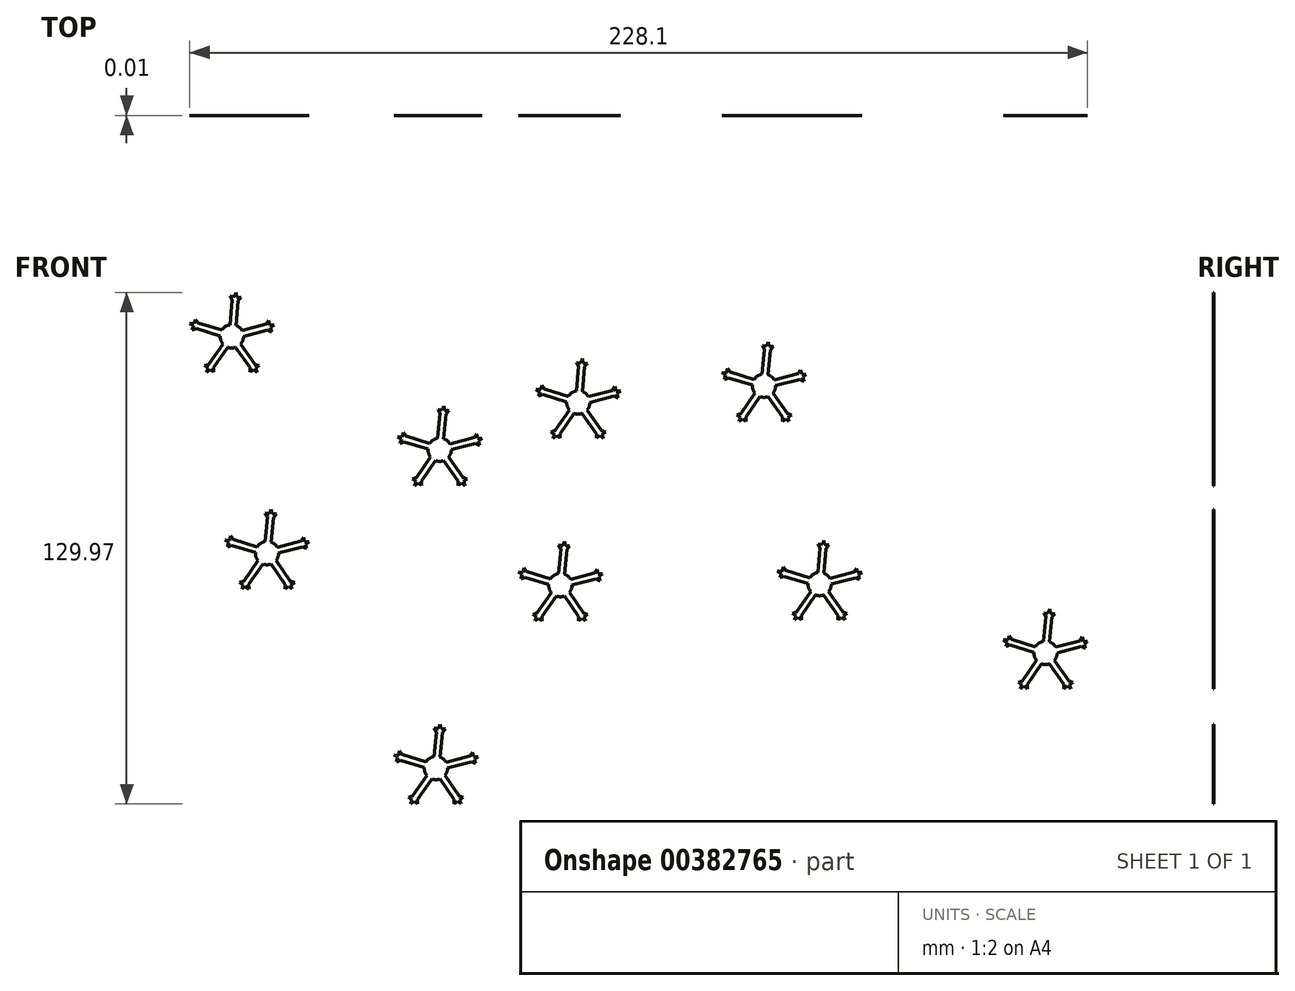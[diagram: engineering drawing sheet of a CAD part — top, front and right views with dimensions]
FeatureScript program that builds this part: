
annotation { "Feature Type Name" : "Feature", "Feature Type Description" : "" }
export const myFeature = defineFeature(function(context is Context, id is Id, definition is map)
    precondition{}
    {
        {
            var Q0;
            Q0=qCreatedBy(makeId("Front.planeOp"),FACE);
            var sketch = newSketch(context, id + "F0", { "sketchPlane" : qUnion([Q0])});
            skLineSegment(sketch, "E0", {"start": v(20.66, -9.4) * mm, "end": v(21.26, -3.1) * mm});
            skLineSegment(sketch, "E1", {"start": v(22.17, -9.55) * mm, "end": v(22.78, -3.26) * mm});
            skLineSegment(sketch, "E2", {"start": v(23.72, -10.87) * mm, "end": v(29.84, -9.26) * mm});
            skLineSegment(sketch, "E3", {"start": v(24.1, -12.34) * mm, "end": v(30.23, -10.74) * mm});
            skLineSegment(sketch, "E4", {"start": v(18.17, -12.22) * mm, "end": v(12.13, -10.36) * mm});
            skLineSegment(sketch, "E5", {"start": v(18.62, -10.76) * mm, "end": v(12.58, -8.9) * mm});
            skLineSegment(sketch, "E6", {"start": v(18.87, -14.25) * mm, "end": v(15.25, -19.44) * mm});
            skLineSegment(sketch, "E7", {"start": v(20.12, -15.12) * mm, "end": v(16.5, -20.31) * mm});
            skLineSegment(sketch, "E8", {"start": v(22.16, -15.12) * mm, "end": v(25.78, -20.31) * mm});
            skLineSegment(sketch, "E9", {"start": v(23.4, -14.25) * mm, "end": v(27.03, -19.44) * mm});
            skArc(sketch, "E10.trimOffspring", {"start": v(23.72, -10.87) * mm, "mid": v(23.06, -10.08) * mm, "end": v(22.17, -9.55) * mm});
            skArc(sketch, "E11.trimOffspring", {"start": v(23.4, -14.25) * mm, "mid": v(23.92, -13.36) * mm, "end": v(24.1, -12.34) * mm});
            skArc(sketch, "E12.trimOffspring", {"start": v(20.12, -15.12) * mm, "mid": v(21.14, -15.3) * mm, "end": v(22.16, -15.12) * mm});
            skArc(sketch, "E13.trimOffspring", {"start": v(18.17, -12.22) * mm, "mid": v(18.33, -13.3) * mm, "end": v(18.87, -14.25) * mm});
            skArc(sketch, "E14.trimOffspring", {"start": v(20.66, -9.4) * mm, "mid": v(19.5, -9.87) * mm, "end": v(18.62, -10.76) * mm});
            skLineSegment(sketch, "E15", {"start": v(21.26, -3.1) * mm, "end": v(22.78, -3.26) * mm});
            skLineSegment(sketch, "E16", {"start": v(29.84, -9.26) * mm, "end": v(30.46, -8.34) * mm});
            skLineSegment(sketch, "E17", {"start": v(30.46, -8.34) * mm, "end": v(30.73, -9.42) * mm});
            skLineSegment(sketch, "E18", {"start": v(30.73, -9.42) * mm, "end": v(31.84, -9.45) * mm});
            skLineSegment(sketch, "E19", {"start": v(31.84, -9.45) * mm, "end": v(30.96, -10.14) * mm});
            skLineSegment(sketch, "E20", {"start": v(30.96, -10.14) * mm, "end": v(31.23, -11.22) * mm});
            skLineSegment(sketch, "E21", {"start": v(31.23, -11.22) * mm, "end": v(30.23, -10.74) * mm});
            skLineSegment(sketch, "E22", {"start": v(21.26, -3.1) * mm, "end": v(20.7, -2.15) * mm});
            skLineSegment(sketch, "E23", {"start": v(20.7, -2.15) * mm, "end": v(21.8, -2.26) * mm});
            skLineSegment(sketch, "E24", {"start": v(21.8, -2.26) * mm, "end": v(22.2, -1.22) * mm});
            skLineSegment(sketch, "E25", {"start": v(22.2, -1.22) * mm, "end": v(22.4, -2.31) * mm});
            skLineSegment(sketch, "E26", {"start": v(22.4, -2.31) * mm, "end": v(23.52, -2.42) * mm});
            skLineSegment(sketch, "E27", {"start": v(23.52, -2.42) * mm, "end": v(22.78, -3.26) * mm});
            skLineSegment(sketch, "E28", {"start": v(25.78, -20.31) * mm, "end": v(27.03, -19.44) * mm});
            skLineSegment(sketch, "E29", {"start": v(27.03, -19.44) * mm, "end": v(28.08, -19.8) * mm});
            skLineSegment(sketch, "E30", {"start": v(28.08, -19.8) * mm, "end": v(27.17, -20.44) * mm});
            skLineSegment(sketch, "E31", {"start": v(27.17, -20.44) * mm, "end": v(27.53, -21.5) * mm});
            skLineSegment(sketch, "E32", {"start": v(27.53, -21.5) * mm, "end": v(26.67, -20.79) * mm});
            skLineSegment(sketch, "E33", {"start": v(26.67, -20.79) * mm, "end": v(25.76, -21.43) * mm});
            skLineSegment(sketch, "E34", {"start": v(25.76, -21.43) * mm, "end": v(25.78, -20.31) * mm});
            skLineSegment(sketch, "E35", {"start": v(29.84, -9.26) * mm, "end": v(30.23, -10.74) * mm});
            skLineSegment(sketch, "E36", {"start": v(12.58, -8.9) * mm, "end": v(12.13, -10.36) * mm});
            skLineSegment(sketch, "E37", {"start": v(15.25, -19.44) * mm, "end": v(16.5, -20.31) * mm});
            skLineSegment(sketch, "E38", {"start": v(12.58, -8.9) * mm, "end": v(11.9, -8) * mm});
            skLineSegment(sketch, "E39", {"start": v(11.9, -8) * mm, "end": v(11.58, -9.07) * mm});
            skLineSegment(sketch, "E40", {"start": v(11.58, -9.07) * mm, "end": v(10.47, -9.05) * mm});
            skLineSegment(sketch, "E41", {"start": v(10.47, -9.05) * mm, "end": v(11.4, -9.65) * mm});
            skLineSegment(sketch, "E42", {"start": v(11.4, -9.65) * mm, "end": v(11.07, -10.72) * mm});
            skLineSegment(sketch, "E43", {"start": v(11.07, -10.72) * mm, "end": v(12.13, -10.36) * mm});
            skLineSegment(sketch, "E44", {"start": v(15.25, -19.44) * mm, "end": v(14.2, -19.8) * mm});
            skLineSegment(sketch, "E45", {"start": v(14.2, -19.8) * mm, "end": v(15.11, -20.44) * mm});
            skLineSegment(sketch, "E46", {"start": v(15.11, -20.44) * mm, "end": v(14.75, -21.5) * mm});
            skLineSegment(sketch, "E47", {"start": v(14.75, -21.5) * mm, "end": v(15.61, -20.79) * mm});
            skLineSegment(sketch, "E48", {"start": v(15.61, -20.79) * mm, "end": v(16.52, -21.43) * mm});
            skLineSegment(sketch, "E49", {"start": v(16.52, -21.43) * mm, "end": v(16.5, -20.31) * mm});
            skLineSegment(sketch, "E50", {"start": v(-26.55, -13.68) * mm, "end": v(-25.95, -7.38) * mm});
            skLineSegment(sketch, "E51", {"start": v(-25.03, -13.82) * mm, "end": v(-24.43, -7.52) * mm});
            skLineSegment(sketch, "E52", {"start": v(-23.49, -15.14) * mm, "end": v(-17.37, -13.53) * mm});
            skLineSegment(sketch, "E53", {"start": v(-23.1, -16.61) * mm, "end": v(-16.98, -15) * mm});
            skLineSegment(sketch, "E54", {"start": v(-29.03, -16.49) * mm, "end": v(-35.08, -14.62) * mm});
            skLineSegment(sketch, "E55", {"start": v(-28.58, -15.03) * mm, "end": v(-34.63, -13.17) * mm});
            skLineSegment(sketch, "E56", {"start": v(-28.33, -18.52) * mm, "end": v(-31.95, -23.7) * mm});
            skLineSegment(sketch, "E57", {"start": v(-27.08, -19.4) * mm, "end": v(-30.7, -24.58) * mm});
            skLineSegment(sketch, "E58", {"start": v(-25.05, -19.4) * mm, "end": v(-21.43, -24.58) * mm});
            skLineSegment(sketch, "E59", {"start": v(-23.8, -18.52) * mm, "end": v(-20.18, -23.7) * mm});
            skArc(sketch, "E60.trimOffspring", {"start": v(-23.49, -15.14) * mm, "mid": v(-24.14, -14.34) * mm, "end": v(-25.03, -13.82) * mm});
            skArc(sketch, "E61.trimOffspring", {"start": v(-23.8, -18.52) * mm, "mid": v(-23.28, -17.63) * mm, "end": v(-23.1, -16.61) * mm});
            skArc(sketch, "E62.trimOffspring", {"start": v(-27.08, -19.4) * mm, "mid": v(-26.07, -19.57) * mm, "end": v(-25.05, -19.4) * mm});
            skArc(sketch, "E63.trimOffspring", {"start": v(-29.03, -16.49) * mm, "mid": v(-28.87, -17.57) * mm, "end": v(-28.33, -18.52) * mm});
            skArc(sketch, "E64.trimOffspring", {"start": v(-26.55, -13.68) * mm, "mid": v(-27.71, -14.13) * mm, "end": v(-28.58, -15.03) * mm});
            skLineSegment(sketch, "E65", {"start": v(-25.95, -7.38) * mm, "end": v(-24.43, -7.52) * mm});
            skLineSegment(sketch, "E66", {"start": v(-17.37, -13.53) * mm, "end": v(-16.75, -12.6) * mm});
            skLineSegment(sketch, "E67", {"start": v(-16.75, -12.6) * mm, "end": v(-16.48, -13.68) * mm});
            skLineSegment(sketch, "E68", {"start": v(-16.48, -13.68) * mm, "end": v(-15.37, -13.72) * mm});
            skLineSegment(sketch, "E69", {"start": v(-15.37, -13.72) * mm, "end": v(-16.24, -14.4) * mm});
            skLineSegment(sketch, "E70", {"start": v(-16.24, -14.4) * mm, "end": v(-15.97, -15.48) * mm});
            skLineSegment(sketch, "E71", {"start": v(-15.97, -15.48) * mm, "end": v(-16.98, -15) * mm});
            skLineSegment(sketch, "E72", {"start": v(-25.95, -7.38) * mm, "end": v(-26.51, -6.42) * mm});
            skLineSegment(sketch, "E73", {"start": v(-26.51, -6.42) * mm, "end": v(-25.4, -6.52) * mm});
            skLineSegment(sketch, "E74", {"start": v(-25.4, -6.52) * mm, "end": v(-25, -5.49) * mm});
            skLineSegment(sketch, "E75", {"start": v(-25, -5.49) * mm, "end": v(-24.8, -6.58) * mm});
            skLineSegment(sketch, "E76", {"start": v(-24.8, -6.58) * mm, "end": v(-23.7, -6.69) * mm});
            skLineSegment(sketch, "E77", {"start": v(-23.7, -6.69) * mm, "end": v(-24.43, -7.52) * mm});
            skLineSegment(sketch, "E78", {"start": v(-21.43, -24.58) * mm, "end": v(-20.18, -23.7) * mm});
            skLineSegment(sketch, "E79", {"start": v(-20.18, -23.7) * mm, "end": v(-19.13, -24.07) * mm});
            skLineSegment(sketch, "E80", {"start": v(-19.13, -24.07) * mm, "end": v(-20.04, -24.7) * mm});
            skLineSegment(sketch, "E81", {"start": v(-20.04, -24.7) * mm, "end": v(-19.68, -25.76) * mm});
            skLineSegment(sketch, "E82", {"start": v(-19.68, -25.76) * mm, "end": v(-20.54, -25.06) * mm});
            skLineSegment(sketch, "E83", {"start": v(-20.54, -25.06) * mm, "end": v(-21.45, -25.7) * mm});
            skLineSegment(sketch, "E84", {"start": v(-21.45, -25.7) * mm, "end": v(-21.43, -24.58) * mm});
            skLineSegment(sketch, "E85", {"start": v(-17.37, -13.53) * mm, "end": v(-16.98, -15) * mm});
            skLineSegment(sketch, "E86", {"start": v(-34.63, -13.17) * mm, "end": v(-35.08, -14.62) * mm});
            skLineSegment(sketch, "E87", {"start": v(-31.95, -23.7) * mm, "end": v(-30.7, -24.58) * mm});
            skLineSegment(sketch, "E88", {"start": v(-34.63, -13.17) * mm, "end": v(-35.3, -12.28) * mm});
            skLineSegment(sketch, "E89", {"start": v(-35.3, -12.28) * mm, "end": v(-35.63, -13.34) * mm});
            skLineSegment(sketch, "E90", {"start": v(-35.63, -13.34) * mm, "end": v(-36.74, -13.31) * mm});
            skLineSegment(sketch, "E91", {"start": v(-36.74, -13.31) * mm, "end": v(-35.8, -13.92) * mm});
            skLineSegment(sketch, "E92", {"start": v(-35.8, -13.92) * mm, "end": v(-36.13, -14.98) * mm});
            skLineSegment(sketch, "E93", {"start": v(-36.13, -14.98) * mm, "end": v(-35.08, -14.62) * mm});
            skLineSegment(sketch, "E94", {"start": v(-31.95, -23.7) * mm, "end": v(-33, -24.07) * mm});
            skLineSegment(sketch, "E95", {"start": v(-33, -24.07) * mm, "end": v(-32.1, -24.7) * mm});
            skLineSegment(sketch, "E96", {"start": v(-32.1, -24.7) * mm, "end": v(-32.46, -25.76) * mm});
            skLineSegment(sketch, "E97", {"start": v(-32.46, -25.76) * mm, "end": v(-31.6, -25.06) * mm});
            skLineSegment(sketch, "E98", {"start": v(-31.6, -25.06) * mm, "end": v(-30.68, -25.7) * mm});
            skLineSegment(sketch, "E99", {"start": v(-30.68, -25.7) * mm, "end": v(-30.7, -24.58) * mm});
            skLineSegment(sketch, "E100", {"start": v(-61.75, -25.68) * mm, "end": v(-61.15, -19.38) * mm});
            skLineSegment(sketch, "E101", {"start": v(-60.24, -25.82) * mm, "end": v(-59.63, -19.52) * mm});
            skLineSegment(sketch, "E102", {"start": v(-58.69, -27.14) * mm, "end": v(-52.57, -25.53) * mm});
            skLineSegment(sketch, "E103", {"start": v(-58.3, -28.61) * mm, "end": v(-52.18, -27) * mm});
            skLineSegment(sketch, "E104", {"start": v(-64.24, -28.49) * mm, "end": v(-70.28, -26.63) * mm});
            skLineSegment(sketch, "E105", {"start": v(-63.79, -27.03) * mm, "end": v(-69.83, -25.17) * mm});
            skLineSegment(sketch, "E106", {"start": v(-63.54, -30.52) * mm, "end": v(-67.16, -35.7) * mm});
            skLineSegment(sketch, "E107", {"start": v(-62.29, -31.4) * mm, "end": v(-65.9, -36.58) * mm});
            skLineSegment(sketch, "E108", {"start": v(-60.25, -31.4) * mm, "end": v(-56.63, -36.58) * mm});
            skLineSegment(sketch, "E109", {"start": v(-59, -30.52) * mm, "end": v(-55.38, -35.7) * mm});
            skArc(sketch, "E110.trimOffspring", {"start": v(-58.69, -27.14) * mm, "mid": v(-59.35, -26.34) * mm, "end": v(-60.24, -25.82) * mm});
            skArc(sketch, "E111.trimOffspring", {"start": v(-59, -30.52) * mm, "mid": v(-58.49, -29.63) * mm, "end": v(-58.3, -28.61) * mm});
            skArc(sketch, "E112.trimOffspring", {"start": v(-62.29, -31.4) * mm, "mid": v(-61.27, -31.57) * mm, "end": v(-60.25, -31.4) * mm});
            skArc(sketch, "E113.trimOffspring", {"start": v(-64.24, -28.49) * mm, "mid": v(-64.08, -29.57) * mm, "end": v(-63.54, -30.52) * mm});
            skArc(sketch, "E114.trimOffspring", {"start": v(-61.75, -25.68) * mm, "mid": v(-62.92, -26.14) * mm, "end": v(-63.79, -27.03) * mm});
            skLineSegment(sketch, "E115", {"start": v(-61.15, -19.38) * mm, "end": v(-59.63, -19.52) * mm});
            skLineSegment(sketch, "E116", {"start": v(-52.57, -25.53) * mm, "end": v(-51.95, -24.6) * mm});
            skLineSegment(sketch, "E117", {"start": v(-51.95, -24.6) * mm, "end": v(-51.68, -25.69) * mm});
            skLineSegment(sketch, "E118", {"start": v(-51.68, -25.69) * mm, "end": v(-50.57, -25.72) * mm});
            skLineSegment(sketch, "E119", {"start": v(-50.57, -25.72) * mm, "end": v(-51.45, -26.4) * mm});
            skLineSegment(sketch, "E120", {"start": v(-51.45, -26.4) * mm, "end": v(-51.18, -27.49) * mm});
            skLineSegment(sketch, "E121", {"start": v(-51.18, -27.49) * mm, "end": v(-52.18, -27) * mm});
            skLineSegment(sketch, "E122", {"start": v(-61.15, -19.38) * mm, "end": v(-61.72, -18.42) * mm});
            skLineSegment(sketch, "E123", {"start": v(-61.72, -18.42) * mm, "end": v(-60.6, -18.53) * mm});
            skLineSegment(sketch, "E124", {"start": v(-60.6, -18.53) * mm, "end": v(-60.2, -17.49) * mm});
            skLineSegment(sketch, "E125", {"start": v(-60.2, -17.49) * mm, "end": v(-60, -18.58) * mm});
            skLineSegment(sketch, "E126", {"start": v(-60, -18.58) * mm, "end": v(-58.9, -18.69) * mm});
            skLineSegment(sketch, "E127", {"start": v(-58.9, -18.69) * mm, "end": v(-59.63, -19.52) * mm});
            skLineSegment(sketch, "E128", {"start": v(-56.63, -36.58) * mm, "end": v(-55.38, -35.7) * mm});
            skLineSegment(sketch, "E129", {"start": v(-55.38, -35.7) * mm, "end": v(-54.33, -36.07) * mm});
            skLineSegment(sketch, "E130", {"start": v(-54.33, -36.07) * mm, "end": v(-55.24, -36.71) * mm});
            skLineSegment(sketch, "E131", {"start": v(-55.24, -36.71) * mm, "end": v(-54.88, -37.76) * mm});
            skLineSegment(sketch, "E132", {"start": v(-54.88, -37.76) * mm, "end": v(-55.74, -37.06) * mm});
            skLineSegment(sketch, "E133", {"start": v(-55.74, -37.06) * mm, "end": v(-56.66, -37.7) * mm});
            skLineSegment(sketch, "E134", {"start": v(-56.66, -37.7) * mm, "end": v(-56.63, -36.58) * mm});
            skLineSegment(sketch, "E135", {"start": v(-52.57, -25.53) * mm, "end": v(-52.18, -27) * mm});
            skLineSegment(sketch, "E136", {"start": v(-69.83, -25.17) * mm, "end": v(-70.28, -26.63) * mm});
            skLineSegment(sketch, "E137", {"start": v(-67.16, -35.7) * mm, "end": v(-65.9, -36.58) * mm});
            skLineSegment(sketch, "E138", {"start": v(-69.83, -25.17) * mm, "end": v(-70.5, -24.28) * mm});
            skLineSegment(sketch, "E139", {"start": v(-70.5, -24.28) * mm, "end": v(-70.83, -25.34) * mm});
            skLineSegment(sketch, "E140", {"start": v(-70.83, -25.34) * mm, "end": v(-71.94, -25.32) * mm});
            skLineSegment(sketch, "E141", {"start": v(-71.94, -25.32) * mm, "end": v(-71, -25.92) * mm});
            skLineSegment(sketch, "E142", {"start": v(-71, -25.92) * mm, "end": v(-71.34, -26.99) * mm});
            skLineSegment(sketch, "E143", {"start": v(-71.34, -26.99) * mm, "end": v(-70.28, -26.63) * mm});
            skLineSegment(sketch, "E144", {"start": v(-67.16, -35.7) * mm, "end": v(-68.2, -36.07) * mm});
            skLineSegment(sketch, "E145", {"start": v(-68.2, -36.07) * mm, "end": v(-67.3, -36.71) * mm});
            skLineSegment(sketch, "E146", {"start": v(-67.3, -36.71) * mm, "end": v(-67.66, -37.76) * mm});
            skLineSegment(sketch, "E147", {"start": v(-67.66, -37.76) * mm, "end": v(-66.8, -37.06) * mm});
            skLineSegment(sketch, "E148", {"start": v(-66.8, -37.06) * mm, "end": v(-65.89, -37.7) * mm});
            skLineSegment(sketch, "E149", {"start": v(-65.89, -37.7) * mm, "end": v(-65.9, -36.58) * mm});
            skLineSegment(sketch, "E150", {"start": v(-114.56, 3.13) * mm, "end": v(-113.96, 9.43) * mm});
            skLineSegment(sketch, "E151", {"start": v(-113.04, 2.98) * mm, "end": v(-112.44, 9.28) * mm});
            skLineSegment(sketch, "E152", {"start": v(-111.5, 1.66) * mm, "end": v(-105.38, 3.27) * mm});
            skLineSegment(sketch, "E153", {"start": v(-111.1, 0.2) * mm, "end": v(-104.99, 1.8) * mm});
            skLineSegment(sketch, "E154", {"start": v(-117.04, 0.32) * mm, "end": v(-123.09, 2.18) * mm});
            skLineSegment(sketch, "E155", {"start": v(-116.6, 1.77) * mm, "end": v(-122.64, 3.63) * mm});
            skLineSegment(sketch, "E156", {"start": v(-116.34, -1.72) * mm, "end": v(-119.96, -6.9) * mm});
            skLineSegment(sketch, "E157", {"start": v(-115.1, -2.59) * mm, "end": v(-118.71, -7.78) * mm});
            skLineSegment(sketch, "E158", {"start": v(-113.06, -2.59) * mm, "end": v(-109.44, -7.78) * mm});
            skLineSegment(sketch, "E159", {"start": v(-111.81, -1.72) * mm, "end": v(-108.2, -6.9) * mm});
            skArc(sketch, "E160.trimOffspring", {"start": v(-111.5, 1.66) * mm, "mid": v(-112.15, 2.46) * mm, "end": v(-113.04, 2.98) * mm});
            skArc(sketch, "E161.trimOffspring", {"start": v(-111.81, -1.72) * mm, "mid": v(-111.3, -0.82) * mm, "end": v(-111.1, 0.2) * mm});
            skArc(sketch, "E162.trimOffspring", {"start": v(-115.1, -2.59) * mm, "mid": v(-114.08, -2.77) * mm, "end": v(-113.06, -2.59) * mm});
            skArc(sketch, "E163.trimOffspring", {"start": v(-117.04, 0.32) * mm, "mid": v(-116.88, -0.77) * mm, "end": v(-116.34, -1.72) * mm});
            skArc(sketch, "E164.trimOffspring", {"start": v(-114.56, 3.13) * mm, "mid": v(-115.72, 2.67) * mm, "end": v(-116.6, 1.77) * mm});
            skLineSegment(sketch, "E165", {"start": v(-113.96, 9.43) * mm, "end": v(-112.44, 9.28) * mm});
            skLineSegment(sketch, "E166", {"start": v(-105.38, 3.27) * mm, "end": v(-104.76, 4.2) * mm});
            skLineSegment(sketch, "E167", {"start": v(-104.76, 4.2) * mm, "end": v(-104.5, 3.12) * mm});
            skLineSegment(sketch, "E168", {"start": v(-104.5, 3.12) * mm, "end": v(-103.38, 3.08) * mm});
            skLineSegment(sketch, "E169", {"start": v(-103.38, 3.08) * mm, "end": v(-104.25, 2.4) * mm});
            skLineSegment(sketch, "E170", {"start": v(-104.25, 2.4) * mm, "end": v(-103.98, 1.32) * mm});
            skLineSegment(sketch, "E171", {"start": v(-103.98, 1.32) * mm, "end": v(-104.99, 1.8) * mm});
            skLineSegment(sketch, "E172", {"start": v(-113.96, 9.43) * mm, "end": v(-114.52, 10.38) * mm});
            skLineSegment(sketch, "E173", {"start": v(-114.52, 10.38) * mm, "end": v(-113.41, 10.28) * mm});
            skLineSegment(sketch, "E174", {"start": v(-113.41, 10.28) * mm, "end": v(-113, 11.32) * mm});
            skLineSegment(sketch, "E175", {"start": v(-113, 11.32) * mm, "end": v(-112.81, 10.22) * mm});
            skLineSegment(sketch, "E176", {"start": v(-112.81, 10.22) * mm, "end": v(-111.7, 10.11) * mm});
            skLineSegment(sketch, "E177", {"start": v(-111.7, 10.11) * mm, "end": v(-112.44, 9.28) * mm});
            skLineSegment(sketch, "E178", {"start": v(-109.44, -7.78) * mm, "end": v(-108.2, -6.9) * mm});
            skLineSegment(sketch, "E179", {"start": v(-108.2, -6.9) * mm, "end": v(-107.14, -7.27) * mm});
            skLineSegment(sketch, "E180", {"start": v(-107.14, -7.27) * mm, "end": v(-108.05, -7.9) * mm});
            skLineSegment(sketch, "E181", {"start": v(-108.05, -7.9) * mm, "end": v(-107.69, -8.96) * mm});
            skLineSegment(sketch, "E182", {"start": v(-107.69, -8.96) * mm, "end": v(-108.55, -8.25) * mm});
            skLineSegment(sketch, "E183", {"start": v(-108.55, -8.25) * mm, "end": v(-109.46, -8.9) * mm});
            skLineSegment(sketch, "E184", {"start": v(-109.46, -8.9) * mm, "end": v(-109.44, -7.78) * mm});
            skLineSegment(sketch, "E185", {"start": v(-105.38, 3.27) * mm, "end": v(-104.99, 1.8) * mm});
            skLineSegment(sketch, "E186", {"start": v(-122.64, 3.63) * mm, "end": v(-123.09, 2.18) * mm});
            skLineSegment(sketch, "E187", {"start": v(-119.96, -6.9) * mm, "end": v(-118.71, -7.78) * mm});
            skLineSegment(sketch, "E188", {"start": v(-122.64, 3.63) * mm, "end": v(-123.3, 4.53) * mm});
            skLineSegment(sketch, "E189", {"start": v(-123.3, 4.53) * mm, "end": v(-123.64, 3.46) * mm});
            skLineSegment(sketch, "E190", {"start": v(-123.64, 3.46) * mm, "end": v(-124.75, 3.49) * mm});
            skLineSegment(sketch, "E191", {"start": v(-124.75, 3.49) * mm, "end": v(-123.81, 2.88) * mm});
            skLineSegment(sketch, "E192", {"start": v(-123.81, 2.88) * mm, "end": v(-124.14, 1.82) * mm});
            skLineSegment(sketch, "E193", {"start": v(-124.14, 1.82) * mm, "end": v(-123.09, 2.18) * mm});
            skLineSegment(sketch, "E194", {"start": v(-119.96, -6.9) * mm, "end": v(-121.02, -7.27) * mm});
            skLineSegment(sketch, "E195", {"start": v(-121.02, -7.27) * mm, "end": v(-120.1, -7.9) * mm});
            skLineSegment(sketch, "E196", {"start": v(-120.1, -7.9) * mm, "end": v(-120.47, -8.96) * mm});
            skLineSegment(sketch, "E197", {"start": v(-120.47, -8.96) * mm, "end": v(-119.6, -8.25) * mm});
            skLineSegment(sketch, "E198", {"start": v(-119.6, -8.25) * mm, "end": v(-118.7, -8.9) * mm});
            skLineSegment(sketch, "E199", {"start": v(-118.7, -8.9) * mm, "end": v(-118.71, -7.78) * mm});
            skLineSegment(sketch, "E200", {"start": v(34.8, -59.81) * mm, "end": v(35.4, -53.52) * mm});
            skLineSegment(sketch, "E201", {"start": v(36.3, -59.96) * mm, "end": v(36.91, -53.66) * mm});
            skLineSegment(sketch, "E202", {"start": v(37.86, -61.28) * mm, "end": v(43.98, -59.67) * mm});
            skLineSegment(sketch, "E203", {"start": v(38.24, -62.75) * mm, "end": v(44.36, -61.14) * mm});
            skLineSegment(sketch, "E204", {"start": v(32.31, -62.63) * mm, "end": v(26.26, -60.76) * mm});
            skLineSegment(sketch, "E205", {"start": v(32.76, -61.17) * mm, "end": v(26.71, -59.3) * mm});
            skLineSegment(sketch, "E206", {"start": v(33, -64.66) * mm, "end": v(29.39, -69.85) * mm});
            skLineSegment(sketch, "E207", {"start": v(34.26, -65.53) * mm, "end": v(30.64, -70.72) * mm});
            skLineSegment(sketch, "E208", {"start": v(36.3, -65.53) * mm, "end": v(39.91, -70.72) * mm});
            skLineSegment(sketch, "E209", {"start": v(37.54, -64.66) * mm, "end": v(41.16, -69.85) * mm});
            skArc(sketch, "E210.trimOffspring", {"start": v(37.86, -61.28) * mm, "mid": v(37.2, -60.48) * mm, "end": v(36.3, -59.96) * mm});
            skArc(sketch, "E211.trimOffspring", {"start": v(37.54, -64.66) * mm, "mid": v(38.06, -63.77) * mm, "end": v(38.24, -62.75) * mm});
            skArc(sketch, "E212.trimOffspring", {"start": v(34.26, -65.53) * mm, "mid": v(35.28, -65.7) * mm, "end": v(36.3, -65.53) * mm});
            skArc(sketch, "E213.trimOffspring", {"start": v(32.31, -62.63) * mm, "mid": v(32.47, -63.7) * mm, "end": v(33, -64.66) * mm});
            skArc(sketch, "E214.trimOffspring", {"start": v(34.8, -59.81) * mm, "mid": v(33.63, -60.27) * mm, "end": v(32.76, -61.17) * mm});
            skLineSegment(sketch, "E215", {"start": v(35.4, -53.52) * mm, "end": v(36.91, -53.66) * mm});
            skLineSegment(sketch, "E216", {"start": v(43.98, -59.67) * mm, "end": v(44.6, -58.74) * mm});
            skLineSegment(sketch, "E217", {"start": v(44.6, -58.74) * mm, "end": v(44.86, -59.82) * mm});
            skLineSegment(sketch, "E218", {"start": v(44.86, -59.82) * mm, "end": v(45.97, -59.86) * mm});
            skLineSegment(sketch, "E219", {"start": v(45.97, -59.86) * mm, "end": v(45.1, -60.54) * mm});
            skLineSegment(sketch, "E220", {"start": v(45.1, -60.54) * mm, "end": v(45.37, -61.62) * mm});
            skLineSegment(sketch, "E221", {"start": v(45.37, -61.62) * mm, "end": v(44.36, -61.14) * mm});
            skLineSegment(sketch, "E222", {"start": v(35.4, -53.52) * mm, "end": v(34.83, -52.56) * mm});
            skLineSegment(sketch, "E223", {"start": v(34.83, -52.56) * mm, "end": v(35.94, -52.66) * mm});
            skLineSegment(sketch, "E224", {"start": v(35.94, -52.66) * mm, "end": v(36.34, -51.63) * mm});
            skLineSegment(sketch, "E225", {"start": v(36.34, -51.63) * mm, "end": v(36.54, -52.72) * mm});
            skLineSegment(sketch, "E226", {"start": v(36.54, -52.72) * mm, "end": v(37.65, -52.83) * mm});
            skLineSegment(sketch, "E227", {"start": v(37.65, -52.83) * mm, "end": v(36.91, -53.66) * mm});
            skLineSegment(sketch, "E228", {"start": v(39.91, -70.72) * mm, "end": v(41.16, -69.85) * mm});
            skLineSegment(sketch, "E229", {"start": v(41.16, -69.85) * mm, "end": v(42.21, -70.21) * mm});
            skLineSegment(sketch, "E230", {"start": v(42.21, -70.21) * mm, "end": v(41.3, -70.85) * mm});
            skLineSegment(sketch, "E231", {"start": v(41.3, -70.85) * mm, "end": v(41.67, -71.9) * mm});
            skLineSegment(sketch, "E232", {"start": v(41.67, -71.9) * mm, "end": v(40.8, -71.2) * mm});
            skLineSegment(sketch, "E233", {"start": v(40.8, -71.2) * mm, "end": v(39.9, -71.83) * mm});
            skLineSegment(sketch, "E234", {"start": v(39.9, -71.83) * mm, "end": v(39.91, -70.72) * mm});
            skLineSegment(sketch, "E235", {"start": v(43.98, -59.67) * mm, "end": v(44.36, -61.14) * mm});
            skLineSegment(sketch, "E236", {"start": v(26.71, -59.3) * mm, "end": v(26.26, -60.76) * mm});
            skLineSegment(sketch, "E237", {"start": v(29.39, -69.85) * mm, "end": v(30.64, -70.72) * mm});
            skLineSegment(sketch, "E238", {"start": v(26.71, -59.3) * mm, "end": v(26.04, -58.42) * mm});
            skLineSegment(sketch, "E239", {"start": v(26.04, -58.42) * mm, "end": v(25.72, -59.48) * mm});
            skLineSegment(sketch, "E240", {"start": v(25.72, -59.48) * mm, "end": v(24.6, -59.45) * mm});
            skLineSegment(sketch, "E241", {"start": v(24.6, -59.45) * mm, "end": v(25.54, -60.06) * mm});
            skLineSegment(sketch, "E242", {"start": v(25.54, -60.06) * mm, "end": v(25.2, -61.12) * mm});
            skLineSegment(sketch, "E243", {"start": v(25.2, -61.12) * mm, "end": v(26.26, -60.76) * mm});
            skLineSegment(sketch, "E244", {"start": v(29.39, -69.85) * mm, "end": v(28.34, -70.21) * mm});
            skLineSegment(sketch, "E245", {"start": v(28.34, -70.21) * mm, "end": v(29.25, -70.85) * mm});
            skLineSegment(sketch, "E246", {"start": v(29.25, -70.85) * mm, "end": v(28.89, -71.9) * mm});
            skLineSegment(sketch, "E247", {"start": v(28.89, -71.9) * mm, "end": v(29.75, -71.2) * mm});
            skLineSegment(sketch, "E248", {"start": v(29.75, -71.2) * mm, "end": v(30.66, -71.83) * mm});
            skLineSegment(sketch, "E249", {"start": v(30.66, -71.83) * mm, "end": v(30.64, -70.72) * mm});
            skLineSegment(sketch, "E250", {"start": v(-31.08, -60.08) * mm, "end": v(-30.48, -53.78) * mm});
            skLineSegment(sketch, "E251", {"start": v(-29.57, -60.23) * mm, "end": v(-28.96, -53.93) * mm});
            skLineSegment(sketch, "E252", {"start": v(-28.02, -61.54) * mm, "end": v(-21.9, -59.94) * mm});
            skLineSegment(sketch, "E253", {"start": v(-27.63, -63.02) * mm, "end": v(-21.51, -61.41) * mm});
            skLineSegment(sketch, "E254", {"start": v(-33.56, -62.9) * mm, "end": v(-39.61, -61.03) * mm});
            skLineSegment(sketch, "E255", {"start": v(-33.12, -61.44) * mm, "end": v(-39.16, -59.57) * mm});
            skLineSegment(sketch, "E256", {"start": v(-32.87, -64.92) * mm, "end": v(-36.49, -70.11) * mm});
            skLineSegment(sketch, "E257", {"start": v(-31.62, -65.8) * mm, "end": v(-35.24, -70.99) * mm});
            skLineSegment(sketch, "E258", {"start": v(-29.58, -65.8) * mm, "end": v(-25.96, -70.99) * mm});
            skLineSegment(sketch, "E259", {"start": v(-28.33, -64.92) * mm, "end": v(-24.71, -70.11) * mm});
            skArc(sketch, "E260.trimOffspring", {"start": v(-28.02, -61.54) * mm, "mid": v(-28.68, -60.75) * mm, "end": v(-29.57, -60.23) * mm});
            skArc(sketch, "E261.trimOffspring", {"start": v(-28.33, -64.92) * mm, "mid": v(-27.81, -64.03) * mm, "end": v(-27.63, -63.02) * mm});
            skArc(sketch, "E262.trimOffspring", {"start": v(-31.62, -65.8) * mm, "mid": v(-30.6, -65.98) * mm, "end": v(-29.58, -65.8) * mm});
            skArc(sketch, "E263.trimOffspring", {"start": v(-33.56, -62.9) * mm, "mid": v(-33.4, -63.97) * mm, "end": v(-32.87, -64.92) * mm});
            skArc(sketch, "E264.trimOffspring", {"start": v(-31.08, -60.08) * mm, "mid": v(-32.25, -60.54) * mm, "end": v(-33.12, -61.44) * mm});
            skLineSegment(sketch, "E265", {"start": v(-30.48, -53.78) * mm, "end": v(-28.96, -53.93) * mm});
            skLineSegment(sketch, "E266", {"start": v(-21.9, -59.94) * mm, "end": v(-21.28, -59) * mm});
            skLineSegment(sketch, "E267", {"start": v(-21.28, -59) * mm, "end": v(-21.01, -60.09) * mm});
            skLineSegment(sketch, "E268", {"start": v(-21.01, -60.09) * mm, "end": v(-19.9, -60.12) * mm});
            skLineSegment(sketch, "E269", {"start": v(-19.9, -60.12) * mm, "end": v(-20.78, -60.81) * mm});
            skLineSegment(sketch, "E270", {"start": v(-20.78, -60.81) * mm, "end": v(-20.5, -61.9) * mm});
            skLineSegment(sketch, "E271", {"start": v(-20.5, -61.9) * mm, "end": v(-21.51, -61.41) * mm});
            skLineSegment(sketch, "E272", {"start": v(-30.48, -53.78) * mm, "end": v(-31.04, -52.82) * mm});
            skLineSegment(sketch, "E273", {"start": v(-31.04, -52.82) * mm, "end": v(-29.94, -52.93) * mm});
            skLineSegment(sketch, "E274", {"start": v(-29.94, -52.93) * mm, "end": v(-29.53, -51.9) * mm});
            skLineSegment(sketch, "E275", {"start": v(-29.53, -51.9) * mm, "end": v(-29.33, -52.99) * mm});
            skLineSegment(sketch, "E276", {"start": v(-29.33, -52.99) * mm, "end": v(-28.22, -53.1) * mm});
            skLineSegment(sketch, "E277", {"start": v(-28.22, -53.1) * mm, "end": v(-28.96, -53.93) * mm});
            skLineSegment(sketch, "E278", {"start": v(-25.96, -70.99) * mm, "end": v(-24.71, -70.11) * mm});
            skLineSegment(sketch, "E279", {"start": v(-24.71, -70.11) * mm, "end": v(-23.66, -70.48) * mm});
            skLineSegment(sketch, "E280", {"start": v(-23.66, -70.48) * mm, "end": v(-24.57, -71.12) * mm});
            skLineSegment(sketch, "E281", {"start": v(-24.57, -71.12) * mm, "end": v(-24.2, -72.17) * mm});
            skLineSegment(sketch, "E282", {"start": v(-24.2, -72.17) * mm, "end": v(-25.07, -71.46) * mm});
            skLineSegment(sketch, "E283", {"start": v(-25.07, -71.46) * mm, "end": v(-25.98, -72.1) * mm});
            skLineSegment(sketch, "E284", {"start": v(-25.98, -72.1) * mm, "end": v(-25.96, -70.99) * mm});
            skLineSegment(sketch, "E285", {"start": v(-21.9, -59.94) * mm, "end": v(-21.51, -61.41) * mm});
            skLineSegment(sketch, "E286", {"start": v(-39.16, -59.57) * mm, "end": v(-39.61, -61.03) * mm});
            skLineSegment(sketch, "E287", {"start": v(-36.49, -70.11) * mm, "end": v(-35.24, -70.99) * mm});
            skLineSegment(sketch, "E288", {"start": v(-39.16, -59.57) * mm, "end": v(-39.83, -58.68) * mm});
            skLineSegment(sketch, "E289", {"start": v(-39.83, -58.68) * mm, "end": v(-40.16, -59.75) * mm});
            skLineSegment(sketch, "E290", {"start": v(-40.16, -59.75) * mm, "end": v(-41.27, -59.72) * mm});
            skLineSegment(sketch, "E291", {"start": v(-41.27, -59.72) * mm, "end": v(-40.34, -60.33) * mm});
            skLineSegment(sketch, "E292", {"start": v(-40.34, -60.33) * mm, "end": v(-40.67, -61.39) * mm});
            skLineSegment(sketch, "E293", {"start": v(-40.67, -61.39) * mm, "end": v(-39.61, -61.03) * mm});
            skLineSegment(sketch, "E294", {"start": v(-36.49, -70.11) * mm, "end": v(-37.54, -70.48) * mm});
            skLineSegment(sketch, "E295", {"start": v(-37.54, -70.48) * mm, "end": v(-36.63, -71.12) * mm});
            skLineSegment(sketch, "E296", {"start": v(-36.63, -71.12) * mm, "end": v(-36.99, -72.17) * mm});
            skLineSegment(sketch, "E297", {"start": v(-36.99, -72.17) * mm, "end": v(-36.13, -71.46) * mm});
            skLineSegment(sketch, "E298", {"start": v(-36.13, -71.46) * mm, "end": v(-35.21, -72.1) * mm});
            skLineSegment(sketch, "E299", {"start": v(-35.21, -72.1) * mm, "end": v(-35.24, -70.99) * mm});
            skLineSegment(sketch, "E300", {"start": v(-105.61, -51.95) * mm, "end": v(-105, -45.65) * mm});
            skLineSegment(sketch, "E301", {"start": v(-104.1, -52.1) * mm, "end": v(-103.5, -45.8) * mm});
            skLineSegment(sketch, "E302", {"start": v(-102.55, -53.41) * mm, "end": v(-96.43, -51.8) * mm});
            skLineSegment(sketch, "E303", {"start": v(-102.16, -54.88) * mm, "end": v(-96.04, -53.28) * mm});
            skLineSegment(sketch, "E304", {"start": v(-108.1, -54.76) * mm, "end": v(-114.14, -52.9) * mm});
            skLineSegment(sketch, "E305", {"start": v(-107.64, -53.3) * mm, "end": v(-113.7, -51.44) * mm});
            skLineSegment(sketch, "E306", {"start": v(-107.4, -56.8) * mm, "end": v(-111.01, -61.98) * mm});
            skLineSegment(sketch, "E307", {"start": v(-106.14, -57.66) * mm, "end": v(-109.76, -62.85) * mm});
            skLineSegment(sketch, "E308", {"start": v(-104.11, -57.66) * mm, "end": v(-100.5, -62.85) * mm});
            skLineSegment(sketch, "E309", {"start": v(-102.86, -56.8) * mm, "end": v(-99.24, -61.98) * mm});
            skArc(sketch, "E310.trimOffspring", {"start": v(-102.55, -53.41) * mm, "mid": v(-103.2, -52.62) * mm, "end": v(-104.1, -52.1) * mm});
            skArc(sketch, "E311.trimOffspring", {"start": v(-102.86, -56.8) * mm, "mid": v(-102.34, -55.9) * mm, "end": v(-102.16, -54.88) * mm});
            skArc(sketch, "E312.trimOffspring", {"start": v(-106.14, -57.66) * mm, "mid": v(-105.13, -57.84) * mm, "end": v(-104.11, -57.66) * mm});
            skArc(sketch, "E313.trimOffspring", {"start": v(-108.1, -54.76) * mm, "mid": v(-107.93, -55.84) * mm, "end": v(-107.4, -56.8) * mm});
            skArc(sketch, "E314.trimOffspring", {"start": v(-105.61, -51.95) * mm, "mid": v(-106.77, -52.4) * mm, "end": v(-107.64, -53.3) * mm});
            skLineSegment(sketch, "E315", {"start": v(-105, -45.65) * mm, "end": v(-103.5, -45.8) * mm});
            skLineSegment(sketch, "E316", {"start": v(-96.43, -51.8) * mm, "end": v(-95.81, -50.88) * mm});
            skLineSegment(sketch, "E317", {"start": v(-95.81, -50.88) * mm, "end": v(-95.54, -51.96) * mm});
            skLineSegment(sketch, "E318", {"start": v(-95.54, -51.96) * mm, "end": v(-94.43, -52) * mm});
            skLineSegment(sketch, "E319", {"start": v(-94.43, -52) * mm, "end": v(-95.3, -52.68) * mm});
            skLineSegment(sketch, "E320", {"start": v(-95.3, -52.68) * mm, "end": v(-95.04, -53.76) * mm});
            skLineSegment(sketch, "E321", {"start": v(-95.04, -53.76) * mm, "end": v(-96.04, -53.28) * mm});
            skLineSegment(sketch, "E322", {"start": v(-105, -45.65) * mm, "end": v(-105.57, -44.7) * mm});
            skLineSegment(sketch, "E323", {"start": v(-105.57, -44.7) * mm, "end": v(-104.46, -44.8) * mm});
            skLineSegment(sketch, "E324", {"start": v(-104.46, -44.8) * mm, "end": v(-104.06, -43.76) * mm});
            skLineSegment(sketch, "E325", {"start": v(-104.06, -43.76) * mm, "end": v(-103.86, -44.85) * mm});
            skLineSegment(sketch, "E326", {"start": v(-103.86, -44.85) * mm, "end": v(-102.75, -44.96) * mm});
            skLineSegment(sketch, "E327", {"start": v(-102.75, -44.96) * mm, "end": v(-103.5, -45.8) * mm});
            skLineSegment(sketch, "E328", {"start": v(-100.5, -62.85) * mm, "end": v(-99.24, -61.98) * mm});
            skLineSegment(sketch, "E329", {"start": v(-99.24, -61.98) * mm, "end": v(-98.19, -62.35) * mm});
            skLineSegment(sketch, "E330", {"start": v(-98.19, -62.35) * mm, "end": v(-99.1, -62.98) * mm});
            skLineSegment(sketch, "E331", {"start": v(-99.1, -62.98) * mm, "end": v(-98.74, -64.03) * mm});
            skLineSegment(sketch, "E332", {"start": v(-98.74, -64.03) * mm, "end": v(-99.6, -63.33) * mm});
            skLineSegment(sketch, "E333", {"start": v(-99.6, -63.33) * mm, "end": v(-100.51, -63.97) * mm});
            skLineSegment(sketch, "E334", {"start": v(-100.51, -63.97) * mm, "end": v(-100.5, -62.85) * mm});
            skLineSegment(sketch, "E335", {"start": v(-96.43, -51.8) * mm, "end": v(-96.04, -53.28) * mm});
            skLineSegment(sketch, "E336", {"start": v(-113.7, -51.44) * mm, "end": v(-114.14, -52.9) * mm});
            skLineSegment(sketch, "E337", {"start": v(-111.01, -61.98) * mm, "end": v(-109.76, -62.85) * mm});
            skLineSegment(sketch, "E338", {"start": v(-113.7, -51.44) * mm, "end": v(-114.36, -50.55) * mm});
            skLineSegment(sketch, "E339", {"start": v(-114.36, -50.55) * mm, "end": v(-114.69, -51.61) * mm});
            skLineSegment(sketch, "E340", {"start": v(-114.69, -51.61) * mm, "end": v(-115.8, -51.59) * mm});
            skLineSegment(sketch, "E341", {"start": v(-115.8, -51.59) * mm, "end": v(-114.87, -52.2) * mm});
            skLineSegment(sketch, "E342", {"start": v(-114.87, -52.2) * mm, "end": v(-115.2, -53.26) * mm});
            skLineSegment(sketch, "E343", {"start": v(-115.2, -53.26) * mm, "end": v(-114.14, -52.9) * mm});
            skLineSegment(sketch, "E344", {"start": v(-111.01, -61.98) * mm, "end": v(-112.07, -62.35) * mm});
            skLineSegment(sketch, "E345", {"start": v(-112.07, -62.35) * mm, "end": v(-111.15, -62.98) * mm});
            skLineSegment(sketch, "E346", {"start": v(-111.15, -62.98) * mm, "end": v(-111.52, -64.03) * mm});
            skLineSegment(sketch, "E347", {"start": v(-111.52, -64.03) * mm, "end": v(-110.66, -63.33) * mm});
            skLineSegment(sketch, "E348", {"start": v(-110.66, -63.33) * mm, "end": v(-109.74, -63.97) * mm});
            skLineSegment(sketch, "E349", {"start": v(-109.74, -63.97) * mm, "end": v(-109.76, -62.85) * mm});
            skLineSegment(sketch, "E350", {"start": v(92.17, -77.3) * mm, "end": v(92.77, -71) * mm});
            skLineSegment(sketch, "E351", {"start": v(93.68, -77.45) * mm, "end": v(94.29, -71.15) * mm});
            skLineSegment(sketch, "E352", {"start": v(95.23, -78.77) * mm, "end": v(101.35, -77.16) * mm});
            skLineSegment(sketch, "E353", {"start": v(95.62, -80.24) * mm, "end": v(101.74, -78.63) * mm});
            skLineSegment(sketch, "E354", {"start": v(89.69, -80.12) * mm, "end": v(83.64, -78.25) * mm});
            skLineSegment(sketch, "E355", {"start": v(90.13, -78.66) * mm, "end": v(84.09, -76.8) * mm});
            skLineSegment(sketch, "E356", {"start": v(90.38, -82.15) * mm, "end": v(86.76, -87.34) * mm});
            skLineSegment(sketch, "E357", {"start": v(91.63, -83.02) * mm, "end": v(88.01, -88.2) * mm});
            skLineSegment(sketch, "E358", {"start": v(93.67, -83.02) * mm, "end": v(97.29, -88.2) * mm});
            skLineSegment(sketch, "E359", {"start": v(94.92, -82.15) * mm, "end": v(98.54, -87.34) * mm});
            skArc(sketch, "E360.trimOffspring", {"start": v(95.23, -78.77) * mm, "mid": v(94.57, -77.97) * mm, "end": v(93.68, -77.45) * mm});
            skArc(sketch, "E361.trimOffspring", {"start": v(94.92, -82.15) * mm, "mid": v(95.44, -81.26) * mm, "end": v(95.62, -80.24) * mm});
            skArc(sketch, "E362.trimOffspring", {"start": v(91.63, -83.02) * mm, "mid": v(92.65, -83.2) * mm, "end": v(93.67, -83.02) * mm});
            skArc(sketch, "E363.trimOffspring", {"start": v(89.69, -80.12) * mm, "mid": v(89.84, -81.2) * mm, "end": v(90.38, -82.15) * mm});
            skArc(sketch, "E364.trimOffspring", {"start": v(92.17, -77.3) * mm, "mid": v(91, -77.76) * mm, "end": v(90.13, -78.66) * mm});
            skLineSegment(sketch, "E365", {"start": v(92.77, -71) * mm, "end": v(94.29, -71.15) * mm});
            skLineSegment(sketch, "E366", {"start": v(101.35, -77.16) * mm, "end": v(101.97, -76.23) * mm});
            skLineSegment(sketch, "E367", {"start": v(101.97, -76.23) * mm, "end": v(102.24, -77.31) * mm});
            skLineSegment(sketch, "E368", {"start": v(102.24, -77.31) * mm, "end": v(103.35, -77.35) * mm});
            skLineSegment(sketch, "E369", {"start": v(103.35, -77.35) * mm, "end": v(102.47, -78.03) * mm});
            skLineSegment(sketch, "E370", {"start": v(102.47, -78.03) * mm, "end": v(102.74, -79.11) * mm});
            skLineSegment(sketch, "E371", {"start": v(102.74, -79.11) * mm, "end": v(101.74, -78.63) * mm});
            skLineSegment(sketch, "E372", {"start": v(92.77, -71) * mm, "end": v(92.2, -70.05) * mm});
            skLineSegment(sketch, "E373", {"start": v(92.2, -70.05) * mm, "end": v(93.31, -70.15) * mm});
            skLineSegment(sketch, "E374", {"start": v(93.31, -70.15) * mm, "end": v(93.72, -69.12) * mm});
            skLineSegment(sketch, "E375", {"start": v(93.72, -69.12) * mm, "end": v(93.92, -70.21) * mm});
            skLineSegment(sketch, "E376", {"start": v(93.92, -70.21) * mm, "end": v(95.03, -70.32) * mm});
            skLineSegment(sketch, "E377", {"start": v(95.03, -70.32) * mm, "end": v(94.29, -71.15) * mm});
            skLineSegment(sketch, "E378", {"start": v(97.29, -88.2) * mm, "end": v(98.54, -87.34) * mm});
            skLineSegment(sketch, "E379", {"start": v(98.54, -87.34) * mm, "end": v(99.59, -87.7) * mm});
            skLineSegment(sketch, "E380", {"start": v(99.59, -87.7) * mm, "end": v(98.68, -88.34) * mm});
            skLineSegment(sketch, "E381", {"start": v(98.68, -88.34) * mm, "end": v(99.04, -89.4) * mm});
            skLineSegment(sketch, "E382", {"start": v(99.04, -89.4) * mm, "end": v(98.18, -88.69) * mm});
            skLineSegment(sketch, "E383", {"start": v(98.18, -88.69) * mm, "end": v(97.27, -89.32) * mm});
            skLineSegment(sketch, "E384", {"start": v(97.27, -89.32) * mm, "end": v(97.29, -88.2) * mm});
            skLineSegment(sketch, "E385", {"start": v(101.35, -77.16) * mm, "end": v(101.74, -78.63) * mm});
            skLineSegment(sketch, "E386", {"start": v(84.09, -76.8) * mm, "end": v(83.64, -78.25) * mm});
            skLineSegment(sketch, "E387", {"start": v(86.76, -87.34) * mm, "end": v(88.01, -88.2) * mm});
            skLineSegment(sketch, "E388", {"start": v(84.09, -76.8) * mm, "end": v(83.42, -75.9) * mm});
            skLineSegment(sketch, "E389", {"start": v(83.42, -75.9) * mm, "end": v(83.1, -76.97) * mm});
            skLineSegment(sketch, "E390", {"start": v(83.1, -76.97) * mm, "end": v(81.98, -76.94) * mm});
            skLineSegment(sketch, "E391", {"start": v(81.98, -76.94) * mm, "end": v(82.91, -77.55) * mm});
            skLineSegment(sketch, "E392", {"start": v(82.91, -77.55) * mm, "end": v(82.58, -78.61) * mm});
            skLineSegment(sketch, "E393", {"start": v(82.58, -78.61) * mm, "end": v(83.64, -78.25) * mm});
            skLineSegment(sketch, "E394", {"start": v(86.76, -87.34) * mm, "end": v(85.71, -87.7) * mm});
            skLineSegment(sketch, "E395", {"start": v(85.71, -87.7) * mm, "end": v(86.62, -88.34) * mm});
            skLineSegment(sketch, "E396", {"start": v(86.62, -88.34) * mm, "end": v(86.26, -89.4) * mm});
            skLineSegment(sketch, "E397", {"start": v(86.26, -89.4) * mm, "end": v(87.12, -88.69) * mm});
            skLineSegment(sketch, "E398", {"start": v(87.12, -88.69) * mm, "end": v(88.04, -89.32) * mm});
            skLineSegment(sketch, "E399", {"start": v(88.04, -89.32) * mm, "end": v(88.01, -88.2) * mm});
            skLineSegment(sketch, "E400", {"start": v(-62.7, -106.56) * mm, "end": v(-62.1, -100.26) * mm});
            skLineSegment(sketch, "E401", {"start": v(-61.19, -106.7) * mm, "end": v(-60.58, -100.4) * mm});
            skLineSegment(sketch, "E402", {"start": v(-59.64, -108.02) * mm, "end": v(-53.52, -106.42) * mm});
            skLineSegment(sketch, "E403", {"start": v(-59.25, -109.5) * mm, "end": v(-53.13, -107.9) * mm});
            skLineSegment(sketch, "E404", {"start": v(-65.18, -109.37) * mm, "end": v(-71.23, -107.51) * mm});
            skLineSegment(sketch, "E405", {"start": v(-64.73, -107.92) * mm, "end": v(-70.78, -106.05) * mm});
            skLineSegment(sketch, "E406", {"start": v(-64.48, -111.4) * mm, "end": v(-68.1, -116.6) * mm});
            skLineSegment(sketch, "E407", {"start": v(-63.23, -112.28) * mm, "end": v(-66.85, -117.47) * mm});
            skLineSegment(sketch, "E408", {"start": v(-61.2, -112.28) * mm, "end": v(-57.58, -117.47) * mm});
            skLineSegment(sketch, "E409", {"start": v(-59.95, -111.4) * mm, "end": v(-56.33, -116.6) * mm});
            skArc(sketch, "E410.trimOffspring", {"start": v(-59.64, -108.02) * mm, "mid": v(-60.3, -107.23) * mm, "end": v(-61.19, -106.7) * mm});
            skArc(sketch, "E411.trimOffspring", {"start": v(-59.95, -111.4) * mm, "mid": v(-59.43, -110.51) * mm, "end": v(-59.25, -109.5) * mm});
            skArc(sketch, "E412.trimOffspring", {"start": v(-63.23, -112.28) * mm, "mid": v(-62.22, -112.46) * mm, "end": v(-61.2, -112.28) * mm});
            skArc(sketch, "E413.trimOffspring", {"start": v(-65.18, -109.37) * mm, "mid": v(-65.02, -110.45) * mm, "end": v(-64.48, -111.4) * mm});
            skArc(sketch, "E414.trimOffspring", {"start": v(-62.7, -106.56) * mm, "mid": v(-63.86, -107.02) * mm, "end": v(-64.73, -107.92) * mm});
            skLineSegment(sketch, "E415", {"start": v(-62.1, -100.26) * mm, "end": v(-60.58, -100.4) * mm});
            skLineSegment(sketch, "E416", {"start": v(-53.52, -106.42) * mm, "end": v(-52.9, -105.49) * mm});
            skLineSegment(sketch, "E417", {"start": v(-52.9, -105.49) * mm, "end": v(-52.63, -106.57) * mm});
            skLineSegment(sketch, "E418", {"start": v(-52.63, -106.57) * mm, "end": v(-51.52, -106.6) * mm});
            skLineSegment(sketch, "E419", {"start": v(-51.52, -106.6) * mm, "end": v(-52.4, -107.3) * mm});
            skLineSegment(sketch, "E420", {"start": v(-52.4, -107.3) * mm, "end": v(-52.13, -108.37) * mm});
            skLineSegment(sketch, "E421", {"start": v(-52.13, -108.37) * mm, "end": v(-53.13, -107.9) * mm});
            skLineSegment(sketch, "E422", {"start": v(-62.1, -100.26) * mm, "end": v(-62.66, -99.3) * mm});
            skLineSegment(sketch, "E423", {"start": v(-62.66, -99.3) * mm, "end": v(-61.55, -99.41) * mm});
            skLineSegment(sketch, "E424", {"start": v(-61.55, -99.41) * mm, "end": v(-61.15, -98.37) * mm});
            skLineSegment(sketch, "E425", {"start": v(-61.15, -98.37) * mm, "end": v(-60.95, -99.47) * mm});
            skLineSegment(sketch, "E426", {"start": v(-60.95, -99.47) * mm, "end": v(-59.84, -99.57) * mm});
            skLineSegment(sketch, "E427", {"start": v(-59.84, -99.57) * mm, "end": v(-60.58, -100.4) * mm});
            skLineSegment(sketch, "E428", {"start": v(-57.58, -117.47) * mm, "end": v(-56.33, -116.6) * mm});
            skLineSegment(sketch, "E429", {"start": v(-56.33, -116.6) * mm, "end": v(-55.28, -116.96) * mm});
            skLineSegment(sketch, "E430", {"start": v(-55.28, -116.96) * mm, "end": v(-56.2, -117.6) * mm});
            skLineSegment(sketch, "E431", {"start": v(-56.2, -117.6) * mm, "end": v(-55.83, -118.65) * mm});
            skLineSegment(sketch, "E432", {"start": v(-55.83, -118.65) * mm, "end": v(-56.69, -117.94) * mm});
            skLineSegment(sketch, "E433", {"start": v(-56.69, -117.94) * mm, "end": v(-57.6, -118.58) * mm});
            skLineSegment(sketch, "E434", {"start": v(-57.6, -118.58) * mm, "end": v(-57.58, -117.47) * mm});
            skLineSegment(sketch, "E435", {"start": v(-53.52, -106.42) * mm, "end": v(-53.13, -107.9) * mm});
            skLineSegment(sketch, "E436", {"start": v(-70.78, -106.05) * mm, "end": v(-71.23, -107.51) * mm});
            skLineSegment(sketch, "E437", {"start": v(-68.1, -116.6) * mm, "end": v(-66.85, -117.47) * mm});
            skLineSegment(sketch, "E438", {"start": v(-70.78, -106.05) * mm, "end": v(-71.45, -105.16) * mm});
            skLineSegment(sketch, "E439", {"start": v(-71.45, -105.16) * mm, "end": v(-71.78, -106.23) * mm});
            skLineSegment(sketch, "E440", {"start": v(-71.78, -106.23) * mm, "end": v(-72.9, -106.2) * mm});
            skLineSegment(sketch, "E441", {"start": v(-72.9, -106.2) * mm, "end": v(-71.96, -106.8) * mm});
            skLineSegment(sketch, "E442", {"start": v(-71.96, -106.8) * mm, "end": v(-72.28, -107.87) * mm});
            skLineSegment(sketch, "E443", {"start": v(-72.28, -107.87) * mm, "end": v(-71.23, -107.51) * mm});
            skLineSegment(sketch, "E444", {"start": v(-68.1, -116.6) * mm, "end": v(-69.16, -116.96) * mm});
            skLineSegment(sketch, "E445", {"start": v(-69.16, -116.96) * mm, "end": v(-68.24, -117.6) * mm});
            skLineSegment(sketch, "E446", {"start": v(-68.24, -117.6) * mm, "end": v(-68.6, -118.65) * mm});
            skLineSegment(sketch, "E447", {"start": v(-68.6, -118.65) * mm, "end": v(-67.75, -117.94) * mm});
            skLineSegment(sketch, "E448", {"start": v(-67.75, -117.94) * mm, "end": v(-66.83, -118.58) * mm});
            skLineSegment(sketch, "E449", {"start": v(-66.83, -118.58) * mm, "end": v(-66.85, -117.47) * mm});
            skSolve(sketch);
        }
        {
            var Q0;
            Q0=makeQuery(id+"F0.imprint","IMPRINT",FACE,{"disambiguationData":[TD([[makeQuery(id+"F0.imprint","IMPRINT",EDGE,{"derivedFrom":sQuery(id+"F0.wireOp",EDGE,"c3b05db5-1c7e-42ce-bddc-29959baa92ca")}),-1.0]])]});
            var Q1;
            Q1=makeQuery(id+"F0.imprint","IMPRINT",FACE,{"disambiguationData":[TD([[makeQuery(id+"F0.imprint","IMPRINT",EDGE,{"derivedFrom":sQuery(id+"F0.wireOp",EDGE,"E0")}),-1.0]])]});
            var Q2;
            Q2=makeQuery(id+"F0.imprint","IMPRINT",FACE,{"disambiguationData":[TD([[makeQuery(id+"F0.imprint","IMPRINT",EDGE,{"derivedFrom":sQuery(id+"F0.wireOp",EDGE,"E50")}),-1.0]])]});
            var Q3;
            Q3=makeQuery(id+"F0.imprint","IMPRINT",FACE,{"disambiguationData":[TD([[makeQuery(id+"F0.imprint","IMPRINT",EDGE,{"derivedFrom":sQuery(id+"F0.wireOp",EDGE,"E100")}),-1.0]])]});
            var Q4;
            Q4=makeQuery(id+"F0.imprint","IMPRINT",FACE,{"disambiguationData":[TD([[makeQuery(id+"F0.imprint","IMPRINT",EDGE,{"derivedFrom":sQuery(id+"F0.wireOp",EDGE,"6603d473-181d-4929-a55f-73914d5b810e")}),1.0]])]});
            var Q5;
            Q5=makeQuery(id+"F0.imprint","IMPRINT",FACE,{"disambiguationData":[TD([[makeQuery(id+"F0.imprint","IMPRINT",EDGE,{"derivedFrom":sQuery(id+"F0.wireOp",EDGE,"cda17845-7b61-46ef-9daf-574dd30e4591")}),-1.0]])]});
            var Q6;
            Q6=makeQuery(id+"F0.imprint","IMPRINT",FACE,{"disambiguationData":[TD([[makeQuery(id+"F0.imprint","IMPRINT",EDGE,{"derivedFrom":sQuery(id+"F0.wireOp",EDGE,"838f05c1-57a7-43bc-a656-f9fe8611e705")}),-1.0]])]});
            var Q7;
            Q7=makeQuery(id+"F0.imprint","IMPRINT",FACE,{"disambiguationData":[TD([[makeQuery(id+"F0.imprint","IMPRINT",EDGE,{"derivedFrom":sQuery(id+"F0.wireOp",EDGE,"9f6fdcf7-3951-4287-823a-e2825e5ab26e")}),-1.0]])]});
            var Q8;
            Q8=makeQuery(id+"F0.imprint","IMPRINT",FACE,{"disambiguationData":[TD([[makeQuery(id+"F0.imprint","IMPRINT",EDGE,{"derivedFrom":sQuery(id+"F0.wireOp",EDGE,"efe6a7f4-30eb-4c0a-8035-113382120815")}),-1.0]])]});
            var Q9;
            Q9=makeQuery(id+"F0.imprint","IMPRINT",FACE,{"disambiguationData":[TD([[makeQuery(id+"F0.imprint","IMPRINT",EDGE,{"derivedFrom":sQuery(id+"F0.wireOp",EDGE,"0e688399-b101-437f-9594-ffdb57f4e469")}),1.0]])]});
            var Q10;
            Q10=makeQuery(id+"F0.imprint","IMPRINT",FACE,{"disambiguationData":[TD([[makeQuery(id+"F0.imprint","IMPRINT",EDGE,{"derivedFrom":sQuery(id+"F0.wireOp",EDGE,"0ac7cd6a-7275-4916-8e76-ec0cd5d0e35d")}),-1.0]])]});
            var Q11;
            Q11=makeQuery(id+"F0.imprint","IMPRINT",FACE,{"disambiguationData":[TD([[makeQuery(id+"F0.imprint","IMPRINT",EDGE,{"derivedFrom":sQuery(id+"F0.wireOp",EDGE,"190593b0-e9af-4b84-ba19-72fabf0371b4")}),-1.0]])]});
            var Q12;
            Q12=makeQuery(id+"F0.imprint","IMPRINT",FACE,{"disambiguationData":[TD([[makeQuery(id+"F0.imprint","IMPRINT",EDGE,{"derivedFrom":sQuery(id+"F0.wireOp",EDGE,"1c169774-b48a-4fb8-8751-e770e5134214")}),-1.0]])]});
            var Q13;
            Q13=makeQuery(id+"F0.imprint","IMPRINT",FACE,{"disambiguationData":[TD([[makeQuery(id+"F0.imprint","IMPRINT",EDGE,{"derivedFrom":sQuery(id+"F0.wireOp",EDGE,"560650dd-981f-477d-8e21-7115cda35015")}),-1.0]])]});
            var Q14;
            Q14=makeQuery(id+"F0.imprint","IMPRINT",FACE,{"disambiguationData":[TD([[makeQuery(id+"F0.imprint","IMPRINT",EDGE,{"derivedFrom":sQuery(id+"F0.wireOp",EDGE,"6c3e602f-b3af-4a64-ad54-8fa8ab76fbf3")}),-1.0]])]});
            var Q15;
            Q15=makeQuery(id+"F0.imprint","IMPRINT",FACE,{"disambiguationData":[TD([[makeQuery(id+"F0.imprint","IMPRINT",EDGE,{"derivedFrom":sQuery(id+"F0.wireOp",EDGE,"E36")}),-1.0]])]});
            var Q16;
            Q16=makeQuery(id+"F0.imprint","IMPRINT",FACE,{"disambiguationData":[TD([[makeQuery(id+"F0.imprint","IMPRINT",EDGE,{"derivedFrom":sQuery(id+"F0.wireOp",EDGE,"E15")}),1.0]])]});
            var Q17;
            Q17=makeQuery(id+"F0.imprint","IMPRINT",FACE,{"disambiguationData":[TD([[makeQuery(id+"F0.imprint","IMPRINT",EDGE,{"derivedFrom":sQuery(id+"F0.wireOp",EDGE,"E16")}),-1.0]])]});
            var Q18;
            Q18=makeQuery(id+"F0.imprint","IMPRINT",FACE,{"disambiguationData":[TD([[makeQuery(id+"F0.imprint","IMPRINT",EDGE,{"derivedFrom":sQuery(id+"F0.wireOp",EDGE,"E28")}),-1.0]])]});
            var Q19;
            Q19=makeQuery(id+"F0.imprint","IMPRINT",FACE,{"disambiguationData":[TD([[makeQuery(id+"F0.imprint","IMPRINT",EDGE,{"derivedFrom":sQuery(id+"F0.wireOp",EDGE,"E37")}),-1.0]])]});
            var Q20;
            Q20=makeQuery(id+"F0.imprint","IMPRINT",FACE,{"disambiguationData":[TD([[makeQuery(id+"F0.imprint","IMPRINT",EDGE,{"derivedFrom":sQuery(id+"F0.wireOp",EDGE,"E78")}),-1.0]])]});
            var Q21;
            Q21=makeQuery(id+"F0.imprint","IMPRINT",FACE,{"disambiguationData":[TD([[makeQuery(id+"F0.imprint","IMPRINT",EDGE,{"derivedFrom":sQuery(id+"F0.wireOp",EDGE,"E87")}),-1.0]])]});
            var Q22;
            Q22=makeQuery(id+"F0.imprint","IMPRINT",FACE,{"disambiguationData":[TD([[makeQuery(id+"F0.imprint","IMPRINT",EDGE,{"derivedFrom":sQuery(id+"F0.wireOp",EDGE,"E86")}),-1.0]])]});
            var Q23;
            Q23=makeQuery(id+"F0.imprint","IMPRINT",FACE,{"disambiguationData":[TD([[makeQuery(id+"F0.imprint","IMPRINT",EDGE,{"derivedFrom":sQuery(id+"F0.wireOp",EDGE,"E65")}),1.0]])]});
            var Q24;
            Q24=makeQuery(id+"F0.imprint","IMPRINT",FACE,{"disambiguationData":[TD([[makeQuery(id+"F0.imprint","IMPRINT",EDGE,{"derivedFrom":sQuery(id+"F0.wireOp",EDGE,"E66")}),-1.0]])]});
            var Q25;
            Q25=makeQuery(id+"F0.imprint","IMPRINT",FACE,{"disambiguationData":[TD([[makeQuery(id+"F0.imprint","IMPRINT",EDGE,{"derivedFrom":sQuery(id+"F0.wireOp",EDGE,"E116")}),-1.0]])]});
            var Q26;
            Q26=makeQuery(id+"F0.imprint","IMPRINT",FACE,{"disambiguationData":[TD([[makeQuery(id+"F0.imprint","IMPRINT",EDGE,{"derivedFrom":sQuery(id+"F0.wireOp",EDGE,"E115")}),1.0]])]});
            var Q27;
            Q27=makeQuery(id+"F0.imprint","IMPRINT",FACE,{"disambiguationData":[TD([[makeQuery(id+"F0.imprint","IMPRINT",EDGE,{"derivedFrom":sQuery(id+"F0.wireOp",EDGE,"E136")}),-1.0]])]});
            var Q28;
            Q28=makeQuery(id+"F0.imprint","IMPRINT",FACE,{"disambiguationData":[TD([[makeQuery(id+"F0.imprint","IMPRINT",EDGE,{"derivedFrom":sQuery(id+"F0.wireOp",EDGE,"E128")}),-1.0]])]});
            var Q29;
            Q29=makeQuery(id+"F0.imprint","IMPRINT",FACE,{"disambiguationData":[TD([[makeQuery(id+"F0.imprint","IMPRINT",EDGE,{"derivedFrom":sQuery(id+"F0.wireOp",EDGE,"E137")}),-1.0]])]});
            var Q30;
            Q30=makeQuery(id+"F0.imprint","IMPRINT",FACE,{"disambiguationData":[TD([[makeQuery(id+"F0.imprint","IMPRINT",EDGE,{"derivedFrom":sQuery(id+"F0.wireOp",EDGE,"7012864e-f187-46f2-bdd6-731cc1c92651")}),1.0]])]});
            var Q31;
            Q31=makeQuery(id+"F0.imprint","IMPRINT",FACE,{"disambiguationData":[TD([[makeQuery(id+"F0.imprint","IMPRINT",EDGE,{"derivedFrom":sQuery(id+"F0.wireOp",EDGE,"f1c5a83c-624f-4fde-ba70-d230ac5afabf")}),-1.0]])]});
            var Q32;
            Q32=makeQuery(id+"F0.imprint","IMPRINT",FACE,{"disambiguationData":[TD([[makeQuery(id+"F0.imprint","IMPRINT",EDGE,{"derivedFrom":sQuery(id+"F0.wireOp",EDGE,"1c52ac69-ab37-4656-9e7d-84a600df8f69")}),-1.0]])]});
            var Q33;
            Q33=makeQuery(id+"F0.imprint","IMPRINT",FACE,{"disambiguationData":[TD([[makeQuery(id+"F0.imprint","IMPRINT",EDGE,{"derivedFrom":sQuery(id+"F0.wireOp",EDGE,"55e41387-b90f-481a-9704-85a3d27c2fb4")}),-1.0]])]});
            var Q34;
            Q34=makeQuery(id+"F0.imprint","IMPRINT",FACE,{"disambiguationData":[TD([[makeQuery(id+"F0.imprint","IMPRINT",EDGE,{"derivedFrom":sQuery(id+"F0.wireOp",EDGE,"0d41fe36-00fe-4aad-a352-079745d005e1")}),-1.0]])]});
            var Q35;
            Q35=makeQuery(id+"F0.imprint","IMPRINT",FACE,{"disambiguationData":[TD([[makeQuery(id+"F0.imprint","IMPRINT",EDGE,{"derivedFrom":sQuery(id+"F0.wireOp",EDGE,"1f920cab-18d1-4297-bc0e-3a2bdbb3ec55")}),-1.0]])]});
            var Q36;
            Q36=makeQuery(id+"F0.imprint","IMPRINT",FACE,{"disambiguationData":[TD([[makeQuery(id+"F0.imprint","IMPRINT",EDGE,{"derivedFrom":sQuery(id+"F0.wireOp",EDGE,"E150")}),-1.0]])]});
            var Q37;
            Q37=makeQuery(id+"F0.imprint","IMPRINT",FACE,{"disambiguationData":[TD([[makeQuery(id+"F0.imprint","IMPRINT",EDGE,{"derivedFrom":sQuery(id+"F0.wireOp",EDGE,"E165")}),1.0]])]});
            var Q38;
            Q38=makeQuery(id+"F0.imprint","IMPRINT",FACE,{"disambiguationData":[TD([[makeQuery(id+"F0.imprint","IMPRINT",EDGE,{"derivedFrom":sQuery(id+"F0.wireOp",EDGE,"E166")}),-1.0]])]});
            var Q39;
            Q39=makeQuery(id+"F0.imprint","IMPRINT",FACE,{"disambiguationData":[TD([[makeQuery(id+"F0.imprint","IMPRINT",EDGE,{"derivedFrom":sQuery(id+"F0.wireOp",EDGE,"E186")}),-1.0]])]});
            var Q40;
            Q40=makeQuery(id+"F0.imprint","IMPRINT",FACE,{"disambiguationData":[TD([[makeQuery(id+"F0.imprint","IMPRINT",EDGE,{"derivedFrom":sQuery(id+"F0.wireOp",EDGE,"E187")}),-1.0]])]});
            var Q41;
            Q41=makeQuery(id+"F0.imprint","IMPRINT",FACE,{"disambiguationData":[TD([[makeQuery(id+"F0.imprint","IMPRINT",EDGE,{"derivedFrom":sQuery(id+"F0.wireOp",EDGE,"E178")}),-1.0]])]});
            var Q42;
            Q42=makeQuery(id+"F0.imprint","IMPRINT",FACE,{"disambiguationData":[TD([[makeQuery(id+"F0.imprint","IMPRINT",EDGE,{"derivedFrom":sQuery(id+"F0.wireOp",EDGE,"E300")}),-1.0]])]});
            var Q43;
            Q43=makeQuery(id+"F0.imprint","IMPRINT",FACE,{"disambiguationData":[TD([[makeQuery(id+"F0.imprint","IMPRINT",EDGE,{"derivedFrom":sQuery(id+"F0.wireOp",EDGE,"E315")}),1.0]])]});
            var Q44;
            Q44=makeQuery(id+"F0.imprint","IMPRINT",FACE,{"disambiguationData":[TD([[makeQuery(id+"F0.imprint","IMPRINT",EDGE,{"derivedFrom":sQuery(id+"F0.wireOp",EDGE,"E336")}),-1.0]])]});
            var Q45;
            Q45=makeQuery(id+"F0.imprint","IMPRINT",FACE,{"disambiguationData":[TD([[makeQuery(id+"F0.imprint","IMPRINT",EDGE,{"derivedFrom":sQuery(id+"F0.wireOp",EDGE,"E316")}),-1.0]])]});
            var Q46;
            Q46=makeQuery(id+"F0.imprint","IMPRINT",FACE,{"disambiguationData":[TD([[makeQuery(id+"F0.imprint","IMPRINT",EDGE,{"derivedFrom":sQuery(id+"F0.wireOp",EDGE,"E328")}),-1.0]])]});
            var Q47;
            Q47=makeQuery(id+"F0.imprint","IMPRINT",FACE,{"disambiguationData":[TD([[makeQuery(id+"F0.imprint","IMPRINT",EDGE,{"derivedFrom":sQuery(id+"F0.wireOp",EDGE,"E337")}),-1.0]])]});
            var Q48;
            Q48=makeQuery(id+"F0.imprint","IMPRINT",FACE,{"disambiguationData":[TD([[makeQuery(id+"F0.imprint","IMPRINT",EDGE,{"derivedFrom":sQuery(id+"F0.wireOp",EDGE,"E415")}),1.0]])]});
            var Q49;
            Q49=makeQuery(id+"F0.imprint","IMPRINT",FACE,{"disambiguationData":[TD([[makeQuery(id+"F0.imprint","IMPRINT",EDGE,{"derivedFrom":sQuery(id+"F0.wireOp",EDGE,"E416")}),-1.0]])]});
            var Q50;
            Q50=makeQuery(id+"F0.imprint","IMPRINT",FACE,{"disambiguationData":[TD([[makeQuery(id+"F0.imprint","IMPRINT",EDGE,{"derivedFrom":sQuery(id+"F0.wireOp",EDGE,"E428")}),-1.0]])]});
            var Q51;
            Q51=makeQuery(id+"F0.imprint","IMPRINT",FACE,{"disambiguationData":[TD([[makeQuery(id+"F0.imprint","IMPRINT",EDGE,{"derivedFrom":sQuery(id+"F0.wireOp",EDGE,"E437")}),-1.0]])]});
            var Q52;
            Q52=makeQuery(id+"F0.imprint","IMPRINT",FACE,{"disambiguationData":[TD([[makeQuery(id+"F0.imprint","IMPRINT",EDGE,{"derivedFrom":sQuery(id+"F0.wireOp",EDGE,"E400")}),-1.0]])]});
            var Q53;
            Q53=makeQuery(id+"F0.imprint","IMPRINT",FACE,{"disambiguationData":[TD([[makeQuery(id+"F0.imprint","IMPRINT",EDGE,{"derivedFrom":sQuery(id+"F0.wireOp",EDGE,"E436")}),-1.0]])]});
            var Q54;
            Q54=makeQuery(id+"F0.imprint","IMPRINT",FACE,{"disambiguationData":[TD([[makeQuery(id+"F0.imprint","IMPRINT",EDGE,{"derivedFrom":sQuery(id+"F0.wireOp",EDGE,"E265")}),1.0]])]});
            var Q55;
            Q55=makeQuery(id+"F0.imprint","IMPRINT",FACE,{"disambiguationData":[TD([[makeQuery(id+"F0.imprint","IMPRINT",EDGE,{"derivedFrom":sQuery(id+"F0.wireOp",EDGE,"E250")}),-1.0]])]});
            var Q56;
            Q56=makeQuery(id+"F0.imprint","IMPRINT",FACE,{"disambiguationData":[TD([[makeQuery(id+"F0.imprint","IMPRINT",EDGE,{"derivedFrom":sQuery(id+"F0.wireOp",EDGE,"E266")}),-1.0]])]});
            var Q57;
            Q57=makeQuery(id+"F0.imprint","IMPRINT",FACE,{"disambiguationData":[TD([[makeQuery(id+"F0.imprint","IMPRINT",EDGE,{"derivedFrom":sQuery(id+"F0.wireOp",EDGE,"E278")}),-1.0]])]});
            var Q58;
            Q58=makeQuery(id+"F0.imprint","IMPRINT",FACE,{"disambiguationData":[TD([[makeQuery(id+"F0.imprint","IMPRINT",EDGE,{"derivedFrom":sQuery(id+"F0.wireOp",EDGE,"E287")}),-1.0]])]});
            var Q59;
            Q59=makeQuery(id+"F0.imprint","IMPRINT",FACE,{"disambiguationData":[TD([[makeQuery(id+"F0.imprint","IMPRINT",EDGE,{"derivedFrom":sQuery(id+"F0.wireOp",EDGE,"E286")}),-1.0]])]});
            var Q60;
            Q60=makeQuery(id+"F0.imprint","IMPRINT",FACE,{"disambiguationData":[TD([[makeQuery(id+"F0.imprint","IMPRINT",EDGE,{"derivedFrom":sQuery(id+"F0.wireOp",EDGE,"71273ff7-a868-412b-a81e-161dce5e1bd6")}),-1.0]])]});
            var Q61;
            Q61=makeQuery(id+"F0.imprint","IMPRINT",FACE,{"disambiguationData":[TD([[makeQuery(id+"F0.imprint","IMPRINT",EDGE,{"derivedFrom":sQuery(id+"F0.wireOp",EDGE,"5aaea130-27c3-4fdf-9c76-5340b5e00610")}),1.0]])]});
            var Q62;
            Q62=makeQuery(id+"F0.imprint","IMPRINT",FACE,{"disambiguationData":[TD([[makeQuery(id+"F0.imprint","IMPRINT",EDGE,{"derivedFrom":sQuery(id+"F0.wireOp",EDGE,"6dcd7b7f-d37b-4edf-9cb1-526b8024fc20")}),-1.0]])]});
            var Q63;
            Q63=makeQuery(id+"F0.imprint","IMPRINT",FACE,{"disambiguationData":[TD([[makeQuery(id+"F0.imprint","IMPRINT",EDGE,{"derivedFrom":sQuery(id+"F0.wireOp",EDGE,"d78c6d2c-7fa1-451b-9db1-465272901574")}),-1.0]])]});
            var Q64;
            Q64=makeQuery(id+"F0.imprint","IMPRINT",FACE,{"disambiguationData":[TD([[makeQuery(id+"F0.imprint","IMPRINT",EDGE,{"derivedFrom":sQuery(id+"F0.wireOp",EDGE,"69c72aff-2048-47d2-a22c-848686364850")}),-1.0]])]});
            var Q65;
            Q65=makeQuery(id+"F0.imprint","IMPRINT",FACE,{"disambiguationData":[TD([[makeQuery(id+"F0.imprint","IMPRINT",EDGE,{"derivedFrom":sQuery(id+"F0.wireOp",EDGE,"c5c6d1bc-9df0-4f2e-bd86-b86a139af49e")}),-1.0]])]});
            var Q66;
            Q66=makeQuery(id+"F0.imprint","IMPRINT",FACE,{"disambiguationData":[TD([[makeQuery(id+"F0.imprint","IMPRINT",EDGE,{"derivedFrom":sQuery(id+"F0.wireOp",EDGE,"E200")}),-1.0]])]});
            var Q67;
            Q67=makeQuery(id+"F0.imprint","IMPRINT",FACE,{"disambiguationData":[TD([[makeQuery(id+"F0.imprint","IMPRINT",EDGE,{"derivedFrom":sQuery(id+"F0.wireOp",EDGE,"E215")}),1.0]])]});
            var Q68;
            Q68=makeQuery(id+"F0.imprint","IMPRINT",FACE,{"disambiguationData":[TD([[makeQuery(id+"F0.imprint","IMPRINT",EDGE,{"derivedFrom":sQuery(id+"F0.wireOp",EDGE,"E216")}),-1.0]])]});
            var Q69;
            Q69=makeQuery(id+"F0.imprint","IMPRINT",FACE,{"disambiguationData":[TD([[makeQuery(id+"F0.imprint","IMPRINT",EDGE,{"derivedFrom":sQuery(id+"F0.wireOp",EDGE,"E228")}),-1.0]])]});
            var Q70;
            Q70=makeQuery(id+"F0.imprint","IMPRINT",FACE,{"disambiguationData":[TD([[makeQuery(id+"F0.imprint","IMPRINT",EDGE,{"derivedFrom":sQuery(id+"F0.wireOp",EDGE,"E237")}),-1.0]])]});
            var Q71;
            Q71=makeQuery(id+"F0.imprint","IMPRINT",FACE,{"disambiguationData":[TD([[makeQuery(id+"F0.imprint","IMPRINT",EDGE,{"derivedFrom":sQuery(id+"F0.wireOp",EDGE,"E236")}),-1.0]])]});
            var Q72;
            Q72=makeQuery(id+"F0.imprint","IMPRINT",FACE,{"disambiguationData":[TD([[makeQuery(id+"F0.imprint","IMPRINT",EDGE,{"derivedFrom":sQuery(id+"F0.wireOp",EDGE,"E350")}),-1.0]])]});
            var Q73;
            Q73=makeQuery(id+"F0.imprint","IMPRINT",FACE,{"disambiguationData":[TD([[makeQuery(id+"F0.imprint","IMPRINT",EDGE,{"derivedFrom":sQuery(id+"F0.wireOp",EDGE,"E365")}),1.0]])]});
            var Q74;
            Q74=makeQuery(id+"F0.imprint","IMPRINT",FACE,{"disambiguationData":[TD([[makeQuery(id+"F0.imprint","IMPRINT",EDGE,{"derivedFrom":sQuery(id+"F0.wireOp",EDGE,"E386")}),-1.0]])]});
            var Q75;
            Q75=makeQuery(id+"F0.imprint","IMPRINT",FACE,{"disambiguationData":[TD([[makeQuery(id+"F0.imprint","IMPRINT",EDGE,{"derivedFrom":sQuery(id+"F0.wireOp",EDGE,"E387")}),-1.0]])]});
            var Q76;
            Q76=makeQuery(id+"F0.imprint","IMPRINT",FACE,{"disambiguationData":[TD([[makeQuery(id+"F0.imprint","IMPRINT",EDGE,{"derivedFrom":sQuery(id+"F0.wireOp",EDGE,"E378")}),-1.0]])]});
            var Q77;
            Q77=makeQuery(id+"F0.imprint","IMPRINT",FACE,{"disambiguationData":[TD([[makeQuery(id+"F0.imprint","IMPRINT",EDGE,{"derivedFrom":sQuery(id+"F0.wireOp",EDGE,"E366")}),-1.0]])]});
            var Q78;
            Q78=makeQuery(id+"F0.imprint","IMPRINT",FACE,{"disambiguationData":[TD([[makeQuery(id+"F0.imprint","IMPRINT",EDGE,{"derivedFrom":sQuery(id+"F0.wireOp",EDGE,"d5c9853f-2590-4488-b51b-0c15bea3ec83")}),-1.0]])]});
            var Q79;
            Q79=makeQuery(id+"F0.imprint","IMPRINT",FACE,{"disambiguationData":[TD([[makeQuery(id+"F0.imprint","IMPRINT",EDGE,{"derivedFrom":sQuery(id+"F0.wireOp",EDGE,"7b6e4ca0-175d-4c23-a193-a453c4bed67a")}),1.0]])]});
            var Q80;
            Q80=makeQuery(id+"F0.imprint","IMPRINT",FACE,{"disambiguationData":[TD([[makeQuery(id+"F0.imprint","IMPRINT",EDGE,{"derivedFrom":sQuery(id+"F0.wireOp",EDGE,"e9003312-b478-4606-bb28-08358f23e1de")}),-1.0]])]});
            var Q81;
            Q81=makeQuery(id+"F0.imprint","IMPRINT",FACE,{"disambiguationData":[TD([[makeQuery(id+"F0.imprint","IMPRINT",EDGE,{"derivedFrom":sQuery(id+"F0.wireOp",EDGE,"bf085d6b-92a4-49b8-b4f3-14740b693b15")}),-1.0]])]});
            var Q82;
            Q82=makeQuery(id+"F0.imprint","IMPRINT",FACE,{"disambiguationData":[TD([[makeQuery(id+"F0.imprint","IMPRINT",EDGE,{"derivedFrom":sQuery(id+"F0.wireOp",EDGE,"9d1faa04-63a2-4b6c-88d1-285fc68c3d58")}),-1.0]])]});
            var Q83;
            Q83=makeQuery(id+"F0.imprint","IMPRINT",FACE,{"disambiguationData":[TD([[makeQuery(id+"F0.imprint","IMPRINT",EDGE,{"derivedFrom":sQuery(id+"F0.wireOp",EDGE,"c09576e8-4dbf-46b8-8f23-fcff0aef2954")}),-1.0]])]});
            var Q84;
            Q84=makeQuery(id+"F0.imprint","IMPRINT",FACE,{"disambiguationData":[TD([[makeQuery(id+"F0.imprint","IMPRINT",EDGE,{"derivedFrom":sQuery(id+"F0.wireOp",EDGE,"70b9ef6a-68ac-48b6-9a50-eccf9648b6b3")}),-1.0]])]});
            var Q85;
            Q85=makeQuery(id+"F0.imprint","IMPRINT",FACE,{"disambiguationData":[TD([[makeQuery(id+"F0.imprint","IMPRINT",EDGE,{"derivedFrom":sQuery(id+"F0.wireOp",EDGE,"0c60d265-6fb5-407c-9c7f-e291dfbab12f")}),1.0]])]});
            var Q86;
            Q86=makeQuery(id+"F0.imprint","IMPRINT",FACE,{"disambiguationData":[TD([[makeQuery(id+"F0.imprint","IMPRINT",EDGE,{"derivedFrom":sQuery(id+"F0.wireOp",EDGE,"08723291-514a-4d44-8f85-6c09401cbd2a")}),-1.0]])]});
            var Q87;
            Q87=makeQuery(id+"F0.imprint","IMPRINT",FACE,{"disambiguationData":[TD([[makeQuery(id+"F0.imprint","IMPRINT",EDGE,{"derivedFrom":sQuery(id+"F0.wireOp",EDGE,"9bbc04e6-dada-441d-80ff-5232e2abaffb")}),-1.0]])]});
            var Q88;
            Q88=makeQuery(id+"F0.imprint","IMPRINT",FACE,{"disambiguationData":[TD([[makeQuery(id+"F0.imprint","IMPRINT",EDGE,{"derivedFrom":sQuery(id+"F0.wireOp",EDGE,"b282cd31-1c10-4f50-9dfa-fde13f2f23ef")}),-1.0]])]});
            var Q89;
            Q89=makeQuery(id+"F0.imprint","IMPRINT",FACE,{"disambiguationData":[TD([[makeQuery(id+"F0.imprint","IMPRINT",EDGE,{"derivedFrom":sQuery(id+"F0.wireOp",EDGE,"a91b33b0-5549-4316-9484-1360b2f78ddd")}),-1.0]])]});
            extrude(context, id + "F1", {"entities" : qUnion([Q0, Q1, Q2, Q3, Q4, Q5, Q6, Q7, Q8, Q9, Q10, Q11, Q12, Q13, Q14, Q15, Q16, Q17, Q18, Q19, Q20, Q21, Q22, Q23, Q24, Q25, Q26, Q27, Q28, Q29, Q30, Q31, Q32, Q33, Q34, Q35, Q36, Q37, Q38, Q39, Q40, Q41, Q42, Q43, Q44, Q45, Q46, Q47, Q48, Q49, Q50, Q51, Q52, Q53, Q54, Q55, Q56, Q57, Q58, Q59, Q60, Q61, Q62, Q63, Q64, Q65, Q66, Q67, Q68, Q69, Q70, Q71, Q72, Q73, Q74, Q75, Q76, Q77, Q78, Q79, Q80, Q81, Q82, Q83, Q84, Q85, Q86, Q87, Q88, Q89]), "depth" : 1 / 101.6 * mm});
        }
    });
